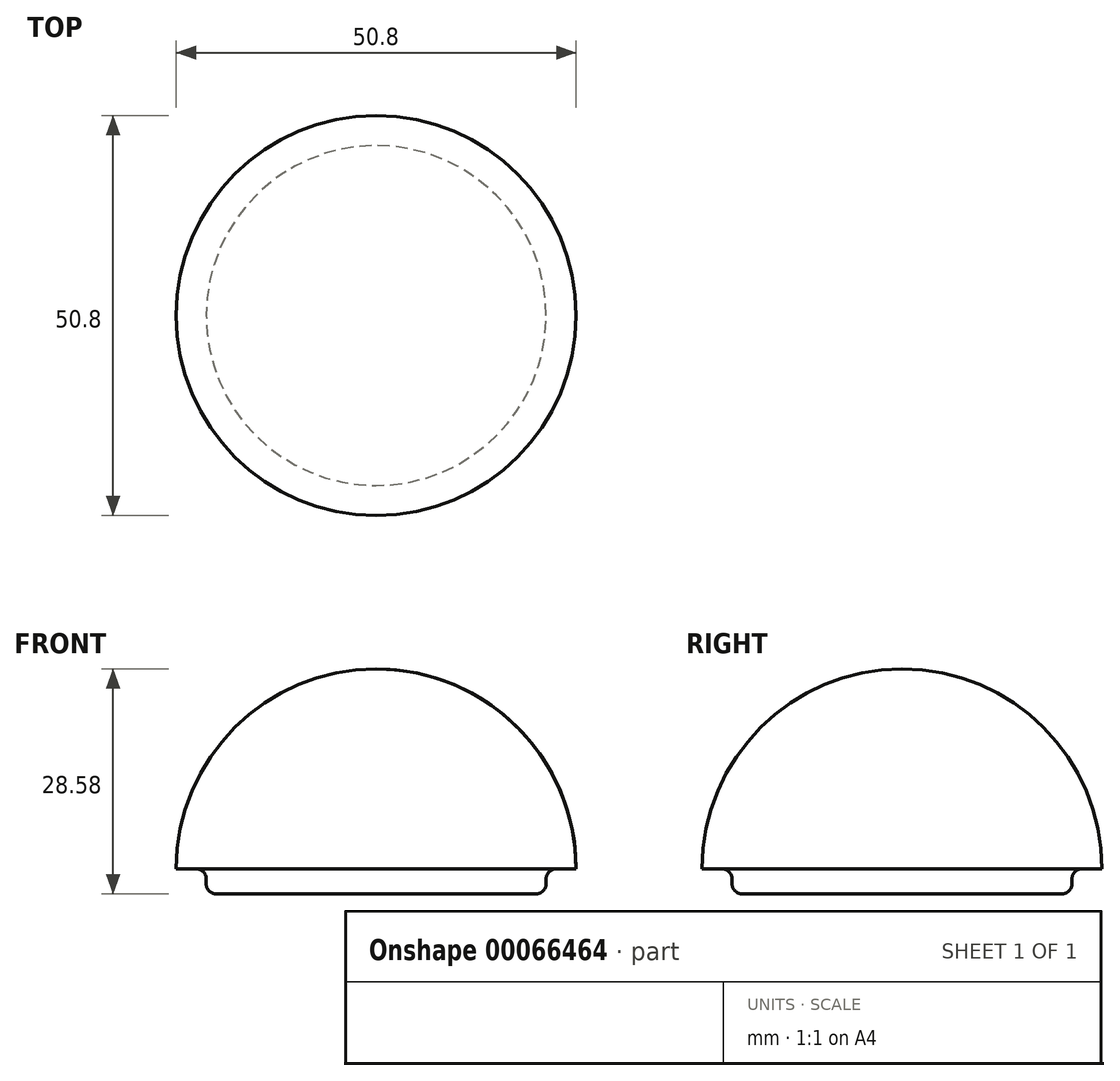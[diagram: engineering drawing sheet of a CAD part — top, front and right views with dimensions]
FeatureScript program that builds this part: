
annotation { "Feature Type Name" : "Feature", "Feature Type Description" : "" }
export const myFeature = defineFeature(function(context is Context, id is Id, definition is map)
    precondition{}
    {
        {
            var Q0;
            Q0=qCreatedBy(makeId("Front.planeOp"),FACE);
            var sketch = newSketch(context, id + "F0", { "sketchPlane" : qUnion([Q0])});
            skLineSegment(sketch, "E0", {"start": v(21.6, -3.17) * mm, "end": v(0, -3.18) * mm});
            skLineSegment(sketch, "E1", {"start": v(0, 25.4) * mm, "end": v(-3.18, 25.4) * mm, "construction": true});
            skLineSegment(sketch, "E2", {"start": v(0, 25.4) * mm, "end": v(0, -3.18) * mm});
            skLineSegment(sketch, "E3", {"start": v(25.4, 0) * mm, "end": v(21.6, 0) * mm});
            skArc(sketch, "E4", {"start": v(25.4, 0) * mm, "mid": v(17.96, 17.96) * mm, "end": v(0, 25.4) * mm});
            skLineSegment(sketch, "E5", {"start": v(21.6, -3.17) * mm, "end": v(21.6, 0) * mm});
            skLineSegment(sketch, "E6", {"start": v(0, 0) * mm, "end": v(0, -3.18) * mm, "construction": true});
            skSolve(sketch);
        }
        {
            var Q0;
            Q0 = qSketchRegion(id + "F0", true);
            var Q1;
            Q1=sQuery(id+"F0.wireOp",EDGE,"E2");
            revolve(context, id + "F1", {"entities" : qUnion([Q0]), "axis" : qUnion([Q1]), "revolveType" : RevolveType.FULL});
        }
        {
            var Q0;
            Q0=makeQuery(id+"F1.opRevolve","SWEPT_EDGE",EDGE,{"disambiguationData":[OSD([sQuery(id+"F0.wireOp",EDGE,"E3"),sQuery(id+"F0.wireOp",EDGE,"E5")])]});
            fillet(context, id + "F2", {"entities" : qUnion([Q0]), "radius" : 1.27 * mm, "tangentPropagation" : true, "allowEdgeOverflow" : false});
        }
        {
            var Q0;
            Q0=makeQuery(id+"F1.opRevolve","SWEPT_EDGE",EDGE,{"disambiguationData":[OSD([sQuery(id+"F0.wireOp",EDGE,"E0"),sQuery(id+"F0.wireOp",EDGE,"E5")])]});
            fillet(context, id + "F3", {"entities" : qUnion([Q0]), "radius" : 1.27 * mm, "tangentPropagation" : true, "allowEdgeOverflow" : false});
        }
    });
